# Revit family: GRAS_HW52NW-20-30 z reduktorem (N)
name_source: partatom
category: Osprzęt hydrauliczny
revit_build: Autodesk Revit 2018 (Build: 20190510_1515(x64)
units: mm (PartAtom-declared; Revit-internal decimal feet)

## family parameters
Obiekt nadrzędny = Powierzchnia
Punkt obliczania pomieszczeń = Nie
Tnij formami wycięć po wczytaniu = Nie
Typ części = Normalny
Współdzielony = Nie
Wymiar okrągłego złącza = Użyj średnicy

## types (2) — shared parameters
Cabinet depth = 250 mm  [stored 0.82021 ft]
Cabinet height = 1010 mm  [stored 3.31365 ft]
Cabinet width = 780 mm  [stored 2.55906 ft]
D1 = 125 mm  [stored 0.410105 ft]
D2 = 125 mm  [stored 0.410105 ft]
DN = 50 mm  [stored 0.164042 ft]
Flow = 246.0 L/s
H1 = 130 mm  [stored 0.426509 ft]
K Factor = 42
Opis = https://gras.pl
Producent = GRAS PPPH
URL = http://www.gras.pl
W1 = 70 mm  [stored 0.229659 ft]
W2 = 40 mm  [stored 0.131234 ft]
zero-valued in all types: Domyślna rzędna

## per-type parameters (varying)
| type | Cabinet material | Model |
| HW-52MW-15/20 z reduktorem, RAL9010 | DC01, RAL9010 | HW-52MW-15/20 + reduktor (N), RAL9010 |
| HW-52MW-15/20 z reduktorem, RAL3000 | DC01, RAL3000 | HW-52NW-15/20 + reduktor (N), RAL3000 |

note: [stored X ft] marks values corroborated as IEEE doubles in the binary element streams (Revit-internal decimal feet)

## geometry (parser evidence)
native form markers: Blend x8
no freeform markers — native parametric forms only
